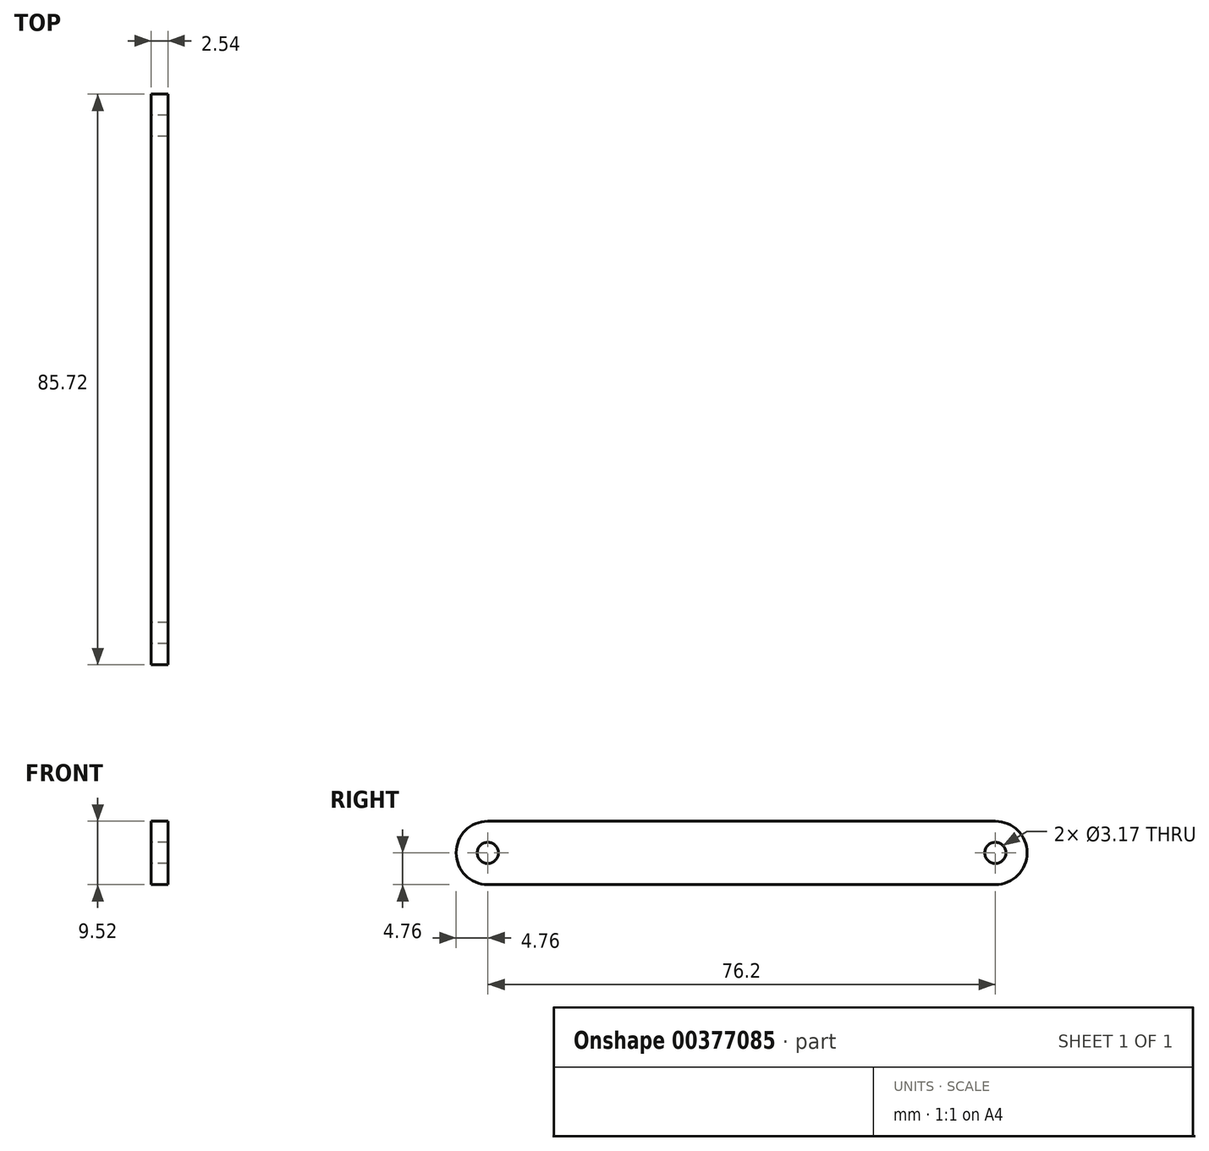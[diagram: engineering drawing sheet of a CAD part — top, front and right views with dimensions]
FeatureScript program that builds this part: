
annotation { "Feature Type Name" : "Feature", "Feature Type Description" : "" }
export const myFeature = defineFeature(function(context is Context, id is Id, definition is map)
    precondition{}
    {
        {
            var Q0;
            Q0=qCreatedBy(makeId("Right.planeOp"),FACE);
            var sketch = newSketch(context, id + "F0", { "sketchPlane" : qUnion([Q0])});
            skLineSegment(sketch, "E0", {"start": v(0, 0) * mm, "end": v(-76.2, 0) * mm, "construction": true});
            skCircle(sketch, "E1", {"center": v(-76.2, 0) * mm, "radius": 1.59 * mm});
            skCircle(sketch, "E2", {"center": v(0, 0) * mm, "radius": 1.59 * mm});
            skArc(sketch, "E3", {"start": v(0, 4.76) * mm, "mid": v(4.76, 0) * mm, "end": v(0, -4.76) * mm});
            skArc(sketch, "E4", {"start": v(-76.2, 4.76) * mm, "mid": v(-80.96, 0) * mm, "end": v(-76.2, -4.76) * mm});
            skLineSegment(sketch, "E5", {"start": v(-76.2, -4.76) * mm, "end": v(0, -4.76) * mm});
            skLineSegment(sketch, "E6", {"start": v(0, 4.76) * mm, "end": v(-76.2, 4.76) * mm});
            skSolve(sketch);
        }
        {
            var Q0;
            Q0 = qSketchRegion(id + "F0", true);
            extrude(context, id + "F1", {"entities" : qUnion([Q0]), "depth" : 2.54 * mm});
        }
    });
